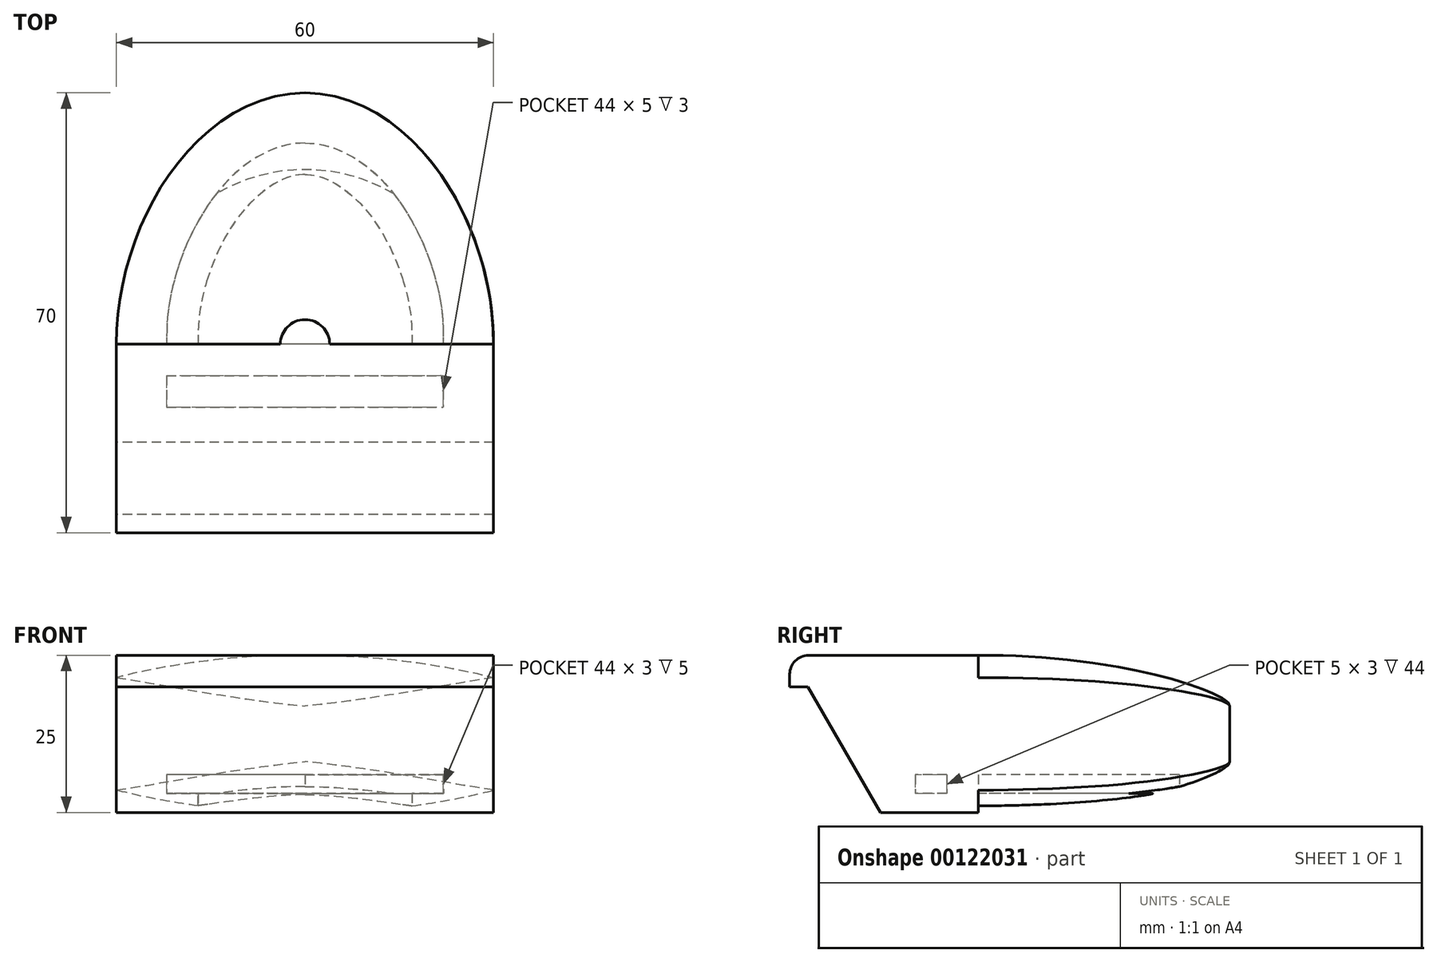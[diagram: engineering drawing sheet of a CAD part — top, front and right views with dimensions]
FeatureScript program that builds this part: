
annotation { "Feature Type Name" : "Feature", "Feature Type Description" : "" }
export const myFeature = defineFeature(function(context is Context, id is Id, definition is map)
    precondition{}
    {
        {
            var Q0;
            Q0=qCreatedBy(makeId("Top.planeOp"),FACE);
            var sketch = newSketch(context, id + "F0", { "sketchPlane" : qUnion([Q0])});
            skLineSegment(sketch, "E0.top", {"start": v(-30, -30) * mm, "end": v(30, -30) * mm});
            skPoint(sketch, "E0.middle", {"position": v(0, 0) * mm});
            skCircle(sketch, "E1", {"center": v(0, 0) * mm, "radius": 30 * mm});
            skPoint(sketch, "E2.visualSharp", {"position": v(-30, -30) * mm});
            skPoint(sketch, "E3.visualSharp", {"position": v(30, -30) * mm});
            skPoint(sketch, "E4", {"position": v(-30, 0) * mm});
            skPoint(sketch, "E5", {"position": v(30, 0) * mm});
            skFitSpline(sketch, "E6", {"points": [v(0, 40) * mm, v(-30, 0) * mm], "startDerivative": vector(-49.89, 0) * mm, "endDerivative": vector(0, -60.15) * mm});
            skFitSpline(sketch, "E7.MirrorCS", {"points": [v(0, 40) * mm, v(30, 0) * mm], "startDerivative": vector(49.89, 0) * mm, "endDerivative": vector(0, -60.15) * mm});
            skLineSegment(sketch, "E8", {"start": v(-30, 0) * mm, "end": v(-30, -30) * mm});
            skLineSegment(sketch, "E9", {"start": v(30, 0) * mm, "end": v(30, -30) * mm});
            skSolve(sketch);
        }
        {
            var Q0;
            Q0=qSketchRegion(id+"F0",true);
            extrude(context, id + "F1", {"entities" : qUnion([Q0]), "endBound" : BoundingType.SYMMETRIC, "depth" : 25 * mm});
        }
        {
            var Q0;
            Q0=qCreatedBy(makeId("Right.planeOp"),FACE);
            var sketch = newSketch(context, id + "F2", { "sketchPlane" : qUnion([Q0])});
            skLineSegment(sketch, "E10", {"start": v(0, 0) * mm, "end": v(-30, 0) * mm});
            skPoint(sketch, "E11", {"position": v(-30, 0) * mm});
            skLineSegment(sketch, "E12", {"start": v(-30, 12.5) * mm, "end": v(-30, -12.5) * mm});
            skLineSegment(sketch, "E13", {"start": v(-30, -12.5) * mm, "end": v(0, -12.5) * mm});
            skLineSegment(sketch, "E14", {"start": v(-30, 12.5) * mm, "end": v(-15.57, -12.5) * mm});
            skLineSegment(sketch, "E15", {"start": v(-30, 7.5) * mm, "end": v(-27.11, 7.5) * mm});
            skSolve(sketch);
        }
        {
            var Q0;
            {var subQ0=sQuery(id+"F2.wireOp",EDGE,"E12");var subQ1=sQuery(id+"F2.wireOp",EDGE,"E10");var subQ2=makeQuery(id+"F2.imprint","INTERSECT",VERTEX,{"derivedFrom":[subQ1,subQ0]});Q0=makeQuery(id+"F2.imprint","IMPRINT",FACE,{"disambiguationData":[TD([[makeQuery(id+"F2.imprint","IMPRINT",EDGE,{"disambiguationData":[TD([[subQ2,1.0]])],"derivedFrom":subQ1}),1.0]])]});}
            var Q1;
            {var subQ0=sQuery(id+"F2.wireOp",EDGE,"E12");var subQ1=sQuery(id+"F2.wireOp",EDGE,"E10");var subQ2=makeQuery(id+"F2.imprint","INTERSECT",VERTEX,{"derivedFrom":[subQ1,subQ0]});Q1=makeQuery(id+"F2.imprint","IMPRINT",FACE,{"disambiguationData":[TD([[makeQuery(id+"F2.imprint","IMPRINT",EDGE,{"disambiguationData":[TD([[subQ2,1.0]])],"derivedFrom":subQ1}),-1.0]])]});}
            extrude(context, id + "F3", {"entities" : qUnion([Q0, Q1]), "operationType" : NewBodyOperationType.REMOVE, "endBound" : BoundingType.SYMMETRIC, "depth" : 60 * mm});
        }
        {
            var Q0;
            Q0=makeQuery(id+"F1.opExtrude","CAP_FACE",FACE,{"disambiguationData":[OSD([sQuery(id+"F0.wireOp",EDGE,"E0.top"),sQuery(id+"F0.wireOp",EDGE,"E6"),sQuery(id+"F0.wireOp",EDGE,"E7.MirrorCS"),sQuery(id+"F0.wireOp",EDGE,"E8"),sQuery(id+"F0.wireOp",EDGE,"E9")])],"isStart":true});
            var sketch = newSketch(context, id + "F4", { "sketchPlane" : qUnion([Q0])});
            skLineSegment(sketch, "E16.bottom", {"start": v(30, 0) * mm, "end": v(-30, 0) * mm});
            skLineSegment(sketch, "E16.top", {"start": v(30, 15.57) * mm, "end": v(-30, 15.57) * mm});
            skLineSegment(sketch, "E16.left", {"start": v(30, 0) * mm, "end": v(30, 15.57) * mm});
            skLineSegment(sketch, "E16.right", {"start": v(-30, 0) * mm, "end": v(-30, 15.57) * mm});
            skFitSpline(sketch, "E17", {"points": [v(0, -40) * mm, v(30, 0) * mm], "startDerivative": vector(49.89, 0) * mm, "endDerivative": vector(0, 60.15) * mm});
            skFitSpline(sketch, "E18.MirrorCS", {"points": [v(0, -40) * mm, v(-30, 0) * mm], "startDerivative": vector(-49.89, 0) * mm, "endDerivative": vector(0, 60.15) * mm});
            skFitSpline(sketch, "E19.0", {"points": [v(0, -32) * mm, v(0.64, -32) * mm, v(1.9, -31.9) * mm, v(3.77, -31.49) * mm, v(5.66, -30.78) * mm, v(8.18, -29.45) * mm, v(11.32, -27.03) * mm, v(14.84, -22.99) * mm, v(17.86, -18) * mm, v(20.18, -12.32) * mm, v(21.66, -6.22) * mm, v(22, -2.06) * mm, v(22, 0) * mm]});
            skFitSpline(sketch, "E19.1", {"points": [v(0, -32) * mm, v(-0.64, -32) * mm, v(-1.9, -31.9) * mm, v(-3.77, -31.49) * mm, v(-5.66, -30.78) * mm, v(-8.18, -29.45) * mm, v(-11.32, -27.03) * mm, v(-14.84, -22.99) * mm, v(-17.86, -18) * mm, v(-20.18, -12.32) * mm, v(-21.66, -6.22) * mm, v(-22, -2.06) * mm, v(-22, 0) * mm]});
            skFitSpline(sketch, "E20.0", {"points": [v(0, -27) * mm, v(0.4, -27) * mm, v(1.15, -26.94) * mm, v(2.33, -26.68) * mm, v(3.59, -26.21) * mm, v(4.94, -25.5) * mm, v(6.36, -24.53) * mm, v(8.32, -22.85) * mm, v(10.76, -20.06) * mm, v(13.36, -15.76) * mm, v(15.4, -10.78) * mm, v(16.7, -5.42) * mm, v(17, -1.78) * mm, v(17, 0) * mm]});
            skFitSpline(sketch, "E20.1", {"points": [v(0, -27) * mm, v(-0.4, -27) * mm, v(-1.15, -26.94) * mm, v(-2.33, -26.68) * mm, v(-3.59, -26.21) * mm, v(-4.94, -25.5) * mm, v(-6.36, -24.53) * mm, v(-8.32, -22.85) * mm, v(-10.76, -20.06) * mm, v(-13.36, -15.76) * mm, v(-15.4, -10.78) * mm, v(-16.7, -5.42) * mm, v(-17, -1.78) * mm, v(-17, 0) * mm]});
            skLineSegment(sketch, "E21.bottom", {"start": v(-22, 0) * mm, "end": v(22, 0) * mm});
            skLineSegment(sketch, "E21.top", {"start": v(-22, 10) * mm, "end": v(22, 10) * mm});
            skLineSegment(sketch, "E21.left", {"start": v(-22, 0) * mm, "end": v(-22, 10) * mm});
            skLineSegment(sketch, "E21.right", {"start": v(22, 0) * mm, "end": v(22, 10) * mm});
            skLineSegment(sketch, "E22", {"start": v(-20.56, -10.51) * mm, "end": v(-15.34, -10.51) * mm});
            skLineSegment(sketch, "E23.MirrorCS", {"start": v(20.56, -10.51) * mm, "end": v(15.34, -10.51) * mm});
            skLineSegment(sketch, "E24.top", {"start": v(-22, 5) * mm, "end": v(22, 5) * mm});
            skLineSegment(sketch, "E24.left", {"start": v(-22, 10) * mm, "end": v(-22, 5) * mm});
            skLineSegment(sketch, "E24.right", {"start": v(22, 10) * mm, "end": v(22, 5) * mm});
            skSolve(sketch);
        }
        {
            var Q0;
            Q0=makeQuery(id+"F4.imprint","IMPRINT",FACE,{"disambiguationData":[TD([[makeQuery(id+"F4.imprint","IMPRINT",EDGE,{"derivedFrom":sQuery(id+"F4.wireOp",EDGE,"E21.top")}),-1.0]])]});
            var Q1;
            {var subQ0=sQuery(id+"F4.wireOp",EDGE,"E21.left");Q1=makeQuery(id+"F4.imprint","IMPRINT",FACE,{"disambiguationData":[TD([[makeQuery(id+"F4.imprint","IMPRINT",EDGE,{"derivedFrom":subQ0}),-1.0]])]});}
            var Q2;
            {var subQ1=sQuery(id+"F4.wireOp",EDGE,"E20.1");var subQ4=sQuery(id+"F4.wireOp",EDGE,"E20.0");var subQ5=makeQuery(id+"F4.imprint","INTERSECT",VERTEX,{"derivedFrom":[subQ4,subQ1]});Q2=makeQuery(id+"F4.imprint","IMPRINT",FACE,{"disambiguationData":[TD([[makeQuery(id+"F4.imprint","IMPRINT",EDGE,{"disambiguationData":[TD([[subQ5,-1.0]])],"derivedFrom":subQ4}),1.0]])]});}
            var Q3;
            {var subQ0=sQuery(id+"F4.wireOp",EDGE,"E21.bottom");var subQ5=sQuery(id+"F4.wireOp",EDGE,"E20.1");var subQ6=makeQuery(id+"F4.imprint","INTERSECT",VERTEX,{"derivedFrom":[subQ5,subQ0]});Q3=makeQuery(id+"F4.imprint","IMPRINT",FACE,{"disambiguationData":[TD([[makeQuery(id+"F4.imprint","IMPRINT",EDGE,{"disambiguationData":[TD([[subQ6,1.0]])],"derivedFrom":subQ5}),1.0]])]});}
            var Q4;
            {var subQ5=sQuery(id+"F4.wireOp",EDGE,"E19.1");var subQ9=sQuery(id+"F4.wireOp",EDGE,"E19.0");var subQ10=makeQuery(id+"F4.imprint","INTERSECT",VERTEX,{"derivedFrom":[subQ9,subQ5]});Q4=makeQuery(id+"F4.imprint","IMPRINT",FACE,{"disambiguationData":[TD([[makeQuery(id+"F4.imprint","IMPRINT",EDGE,{"disambiguationData":[TD([[subQ10,-1.0]])],"derivedFrom":subQ9}),1.0]])]});}
            var Q5;
            {var subQ0=sQuery(id+"F4.wireOp",EDGE,"E21.bottom");var subQ5=sQuery(id+"F4.wireOp",EDGE,"E20.0");var subQ6=makeQuery(id+"F4.imprint","INTERSECT",VERTEX,{"derivedFrom":[subQ5,subQ0]});Q5=makeQuery(id+"F4.imprint","IMPRINT",FACE,{"disambiguationData":[TD([[makeQuery(id+"F4.imprint","IMPRINT",EDGE,{"disambiguationData":[TD([[subQ6,1.0]])],"derivedFrom":subQ5}),-1.0]])]});}
            extrude(context, id + "F5", {"entities" : qUnion([Q0, Q1, Q2, Q3, Q4, Q5]), "operationType" : NewBodyOperationType.REMOVE, "oppositeDirection" : true, "depth" : 6 * mm});
        }
        {
            var Q0;
            {var subQ5=sQuery(id+"F4.wireOp",EDGE,"E19.1");var subQ9=sQuery(id+"F4.wireOp",EDGE,"E19.0");var subQ10=makeQuery(id+"F4.imprint","INTERSECT",VERTEX,{"derivedFrom":[subQ9,subQ5]});Q0=makeQuery(id+"F4.imprint","IMPRINT",FACE,{"disambiguationData":[TD([[makeQuery(id+"F4.imprint","IMPRINT",EDGE,{"disambiguationData":[TD([[subQ10,-1.0]])],"derivedFrom":subQ9}),1.0]])]});}
            var Q1;
            Q1=makeQuery(id+"F4.imprint","IMPRINT",FACE,{"disambiguationData":[TD([[makeQuery(id+"F4.imprint","IMPRINT",EDGE,{"derivedFrom":sQuery(id+"F4.wireOp",EDGE,"E21.top")}),-1.0]])]});
            extrude(context, id + "F6", {"entities" : qUnion([Q0, Q1]), "operationType" : NewBodyOperationType.ADD, "oppositeDirection" : true, "depth" : 3 * mm});
        }
        {
            var Q0;
            Q0=makeQuery(id+"F1.opExtrude","CAP_EDGE",EDGE,{"disambiguationData":[OSD([sQuery(id+"F0.wireOp",EDGE,"E0.top")])],"isStart":false});
            fillet(context, id + "F7", {"entities" : qUnion([Q0]), "radius" : 3 * mm, "tangentPropagation" : true, "allowEdgeOverflow" : false});
        }
        {
            var Q0;
            Q0=qCreatedBy(makeId("Right.planeOp"),FACE);
            var sketch = newSketch(context, id + "F8", { "sketchPlane" : qUnion([Q0])});
            skLineSegment(sketch, "E25", {"start": v(0, 0) * mm, "end": v(0, 18.24) * mm});
            skLineSegment(sketch, "E26", {"start": v(0, 0) * mm, "end": v(40, 0) * mm});
            skFitSpline(sketch, "E27", {"points": [v(0, 12.56) * mm, v(40, 4.41) * mm], "startDerivative": vector(68.19, 0) * mm, "endDerivative": vector(0, -6.71) * mm});
            skLineSegment(sketch, "E28.bottom", {"start": v(0, 18.24) * mm, "end": v(40, 18.24) * mm});
            skLineSegment(sketch, "E28.top", {"start": v(0, 12.56) * mm, "end": v(40, 12.56) * mm});
            skLineSegment(sketch, "E28.left", {"start": v(0, 18.24) * mm, "end": v(0, 12.56) * mm});
            skLineSegment(sketch, "E28.right", {"start": v(40, 18.24) * mm, "end": v(40, 12.56) * mm});
            skLineSegment(sketch, "E29", {"start": v(40, 12.56) * mm, "end": v(40, 4.41) * mm});
            skLineSegment(sketch, "E30.MirrorCS", {"start": v(0, 0) * mm, "end": v(0, -18.24) * mm});
            skLineSegment(sketch, "E31.MirrorCS", {"start": v(0, -18.24) * mm, "end": v(40, -18.24) * mm});
            skLineSegment(sketch, "E32.MirrorCS", {"start": v(40, -18.24) * mm, "end": v(40, -12.56) * mm});
            skFitSpline(sketch, "E33.MirrorCS", {"points": [v(0, -12.56) * mm, v(40, -4.41) * mm], "startDerivative": vector(68.19, 0) * mm, "endDerivative": vector(0, 6.71) * mm});
            skLineSegment(sketch, "E34", {"start": v(40, -4.41) * mm, "end": v(40, -12.56) * mm});
            skSolve(sketch);
        }
        {
            var Q0;
            Q0=makeQuery(id+"F8.imprint","IMPRINT",FACE,{"disambiguationData":[TD([[makeQuery(id+"F8.imprint","IMPRINT",EDGE,{"derivedFrom":sQuery(id+"F8.wireOp",EDGE,"E28.bottom")}),-1.0]])]});
            var Q1;
            Q1=makeQuery(id+"F8.imprint","IMPRINT",FACE,{"disambiguationData":[TD([[makeQuery(id+"F8.imprint","IMPRINT",EDGE,{"derivedFrom":sQuery(id+"F8.wireOp",EDGE,"E27")}),1.0]])]});
            var Q2;
            {var subQ0=sQuery(id+"F8.wireOp",EDGE,"E31.MirrorCS");Q2=makeQuery(id+"F8.imprint","IMPRINT",FACE,{"disambiguationData":[TD([[makeQuery(id+"F8.imprint","IMPRINT",EDGE,{"derivedFrom":subQ0}),1.0]])]});}
            var Q3;
            {var subQ0=sQuery(id+"F8.wireOp",EDGE,"E31.MirrorCS");Q3=makeQuery(id+"F8.imprint","IMPRINT",FACE,{"disambiguationData":[TD([[makeQuery(id+"F8.imprint","IMPRINT",EDGE,{"derivedFrom":subQ0}),1.0]])]});}
            var Q4;
            Q4=sQuery(id+"F8.wireOp",EDGE,"E25");
            revolve(context, id + "F9", {"operationType" : NewBodyOperationType.REMOVE, "entities" : qUnion([Q0, Q1, Q2, Q3]), "axis" : qUnion([Q4]), "revolveType" : RevolveType.SYMMETRIC, "oppositeDirection" : true, "angle" : 180 * degree});
        }
    });
